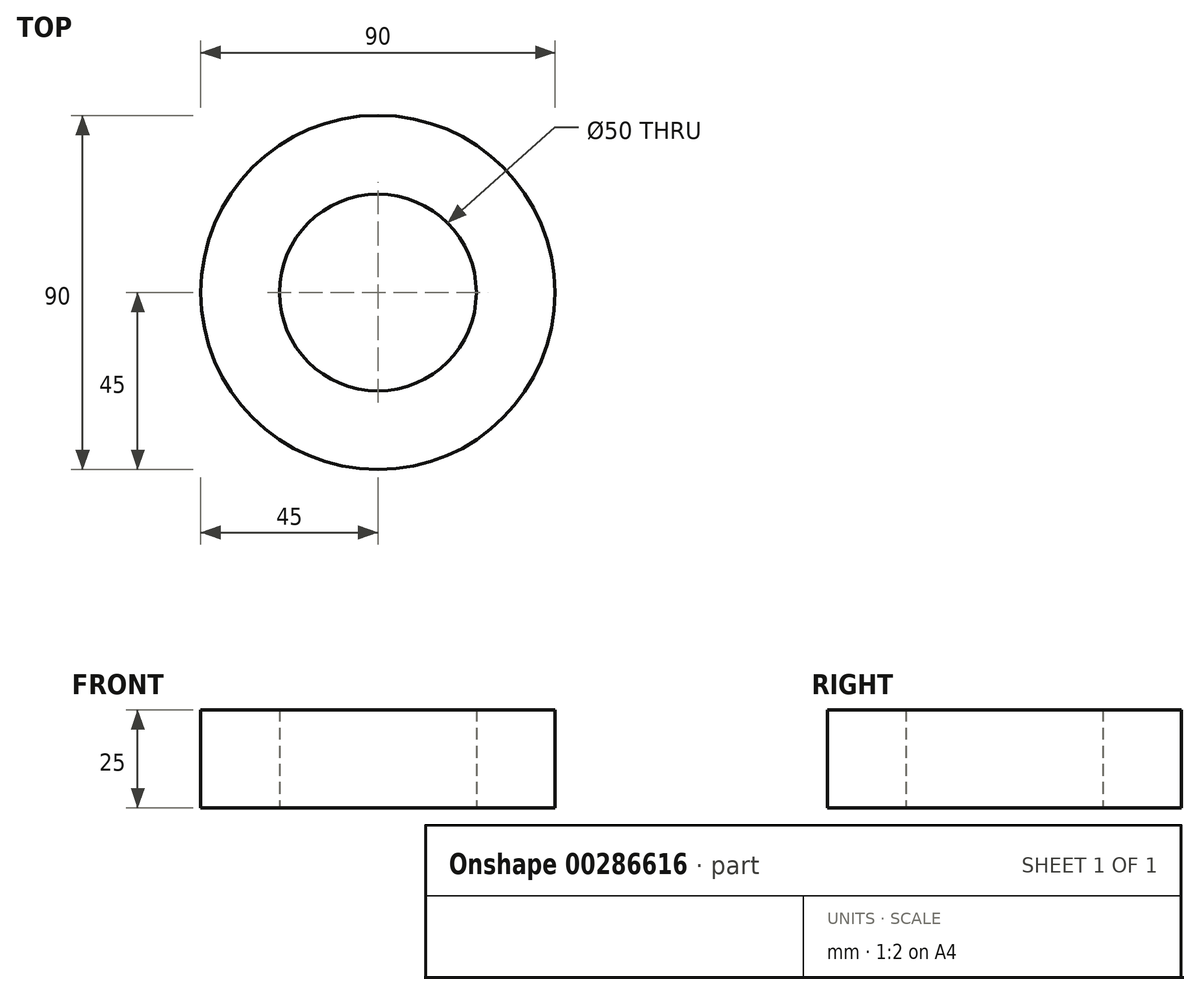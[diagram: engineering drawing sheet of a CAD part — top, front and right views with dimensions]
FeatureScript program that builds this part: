
annotation { "Feature Type Name" : "Feature", "Feature Type Description" : "" }
export const myFeature = defineFeature(function(context is Context, id is Id, definition is map)
    precondition{}
    {
        {
            var Q0;
            Q0=qCreatedBy(makeId("Top.planeOp"),FACE);
            var sketch = newSketch(context, id + "F0", { "sketchPlane" : qUnion([Q0])});
            skCircle(sketch, "E0", {"center": v(0, 0) * mm, "radius": 45 * mm});
            skCircle(sketch, "E1", {"center": v(0, 0) * mm, "radius": 25 * mm});
            skSolve(sketch);
        }
        {
            var Q0;
            Q0=makeQuery(id+"F0.imprint","IMPRINT",FACE,{"disambiguationData":[TD([[makeQuery(id+"F0.imprint","IMPRINT",EDGE,{"derivedFrom":sQuery(id+"F0.wireOp",EDGE,"E0")}),1.0]])]});
            extrude(context, id + "F1", {"entities" : qUnion([Q0]), "depth" : 25 * mm});
        }
    });
